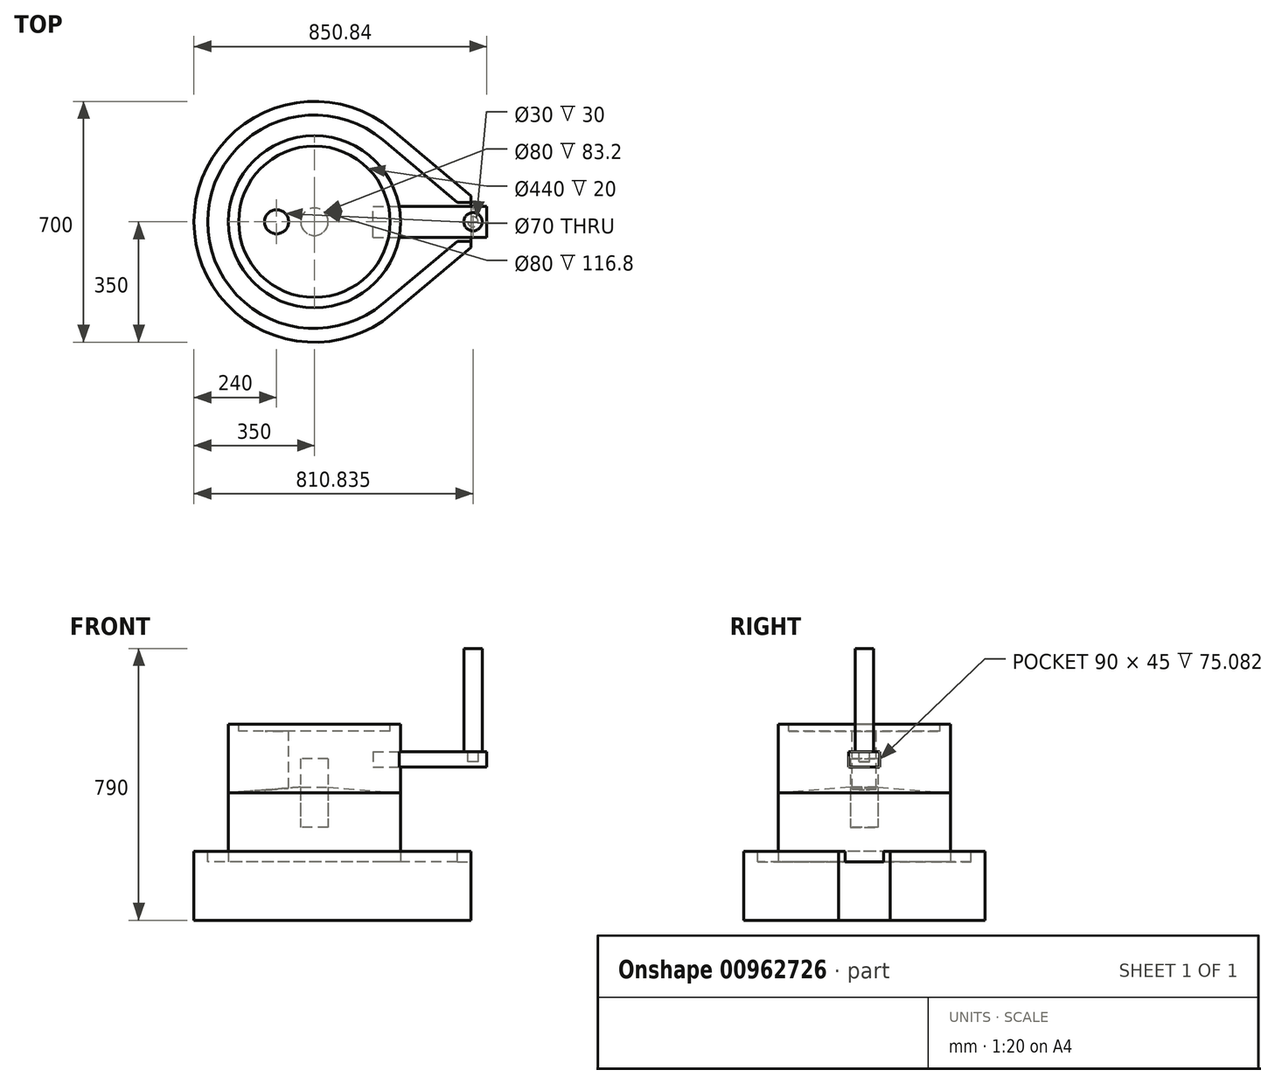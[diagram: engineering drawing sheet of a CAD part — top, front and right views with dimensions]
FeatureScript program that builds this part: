
annotation { "Feature Type Name" : "Feature", "Feature Type Description" : "" }
export const myFeature = defineFeature(function(context is Context, id is Id, definition is map)
    precondition{}
    {
        {
            var Q0;
            Q0=qCreatedBy(makeId("Top.planeOp"),FACE);
            var sketch = newSketch(context, id + "F0", { "sketchPlane" : qUnion([Q0])});
            skCircle(sketch, "E0", {"center": v(0, 0) * mm, "radius": 350 * mm});
            skLineSegment(sketch, "E1", {"start": v(454.84, 0) * mm, "end": v(454.84, 75) * mm});
            skLineSegment(sketch, "E2", {"start": v(454.84, 75) * mm, "end": v(225.14, 267.98) * mm});
            skLineSegment(sketch, "E3.MirrorCS", {"start": v(454.84, -75) * mm, "end": v(225.14, -267.98) * mm});
            skLineSegment(sketch, "E4.MirrorCS", {"start": v(454.84, 0) * mm, "end": v(454.84, -75) * mm});
            skSolve(sketch);
        }
        {
            var Q0;
            Q0=qSketchRegion(id+"F0",true);
            extrude(context, id + "F1", {"entities" : qUnion([Q0]), "depth" : 200 * mm, "offsetDistance" : 25 * mm});
        }
        {
            var Q0;
            Q0=makeQuery(id+"F1.opExtrude","CAP_FACE",FACE,{"disambiguationData":[OSD([sQuery(id+"F0.wireOp",EDGE,"E0"),sQuery(id+"F0.wireOp",EDGE,"E1"),sQuery(id+"F0.wireOp",EDGE,"E2"),sQuery(id+"F0.wireOp",EDGE,"E3.MirrorCS"),sQuery(id+"F0.wireOp",EDGE,"E4.MirrorCS")])],"isStart":false});
            var sketch = newSketch(context, id + "F2", { "sketchPlane" : qUnion([Q0])});
            skArc(sketch, "E5.0", {"start": v(199.4, 237.35) * mm, "mid": v(-310, 0) * mm, "end": v(199.4, -237.35) * mm});
            skLineSegment(sketch, "E5.1", {"start": v(414.84, 56.36) * mm, "end": v(199.4, 237.35) * mm});
            skLineSegment(sketch, "E5.3", {"start": v(199.4, -237.35) * mm, "end": v(414.84, -56.36) * mm});
            skLineSegment(sketch, "E6", {"start": v(414.84, 56.36) * mm, "end": v(454.84, 56.36) * mm});
            skLineSegment(sketch, "E7", {"start": v(454.84, 56.36) * mm, "end": v(454.84, -56.36) * mm});
            skLineSegment(sketch, "E8", {"start": v(454.84, -56.36) * mm, "end": v(414.84, -56.36) * mm});
            skSolve(sketch);
        }
        {
            var Q0;
            Q0=qSketchRegion(id+"F2",true);
            extrude(context, id + "F3", {"entities" : qUnion([Q0]), "operationType" : NewBodyOperationType.REMOVE, "oppositeDirection" : true, "depth" : 30 * mm, "offsetDistance" : 25 * mm});
        }
        {
            var Q0;
            Q0=makeQuery(id+"F3.boolean.opBoolean","COPY",FACE,{"derivedFrom":makeQuery(id+"F3.opExtrude","CAP_FACE",FACE,{"disambiguationData":[OSD([sQuery(id+"F2.wireOp",EDGE,"E5.0"),sQuery(id+"F2.wireOp",EDGE,"E5.1"),sQuery(id+"F2.wireOp",EDGE,"E5.3"),sQuery(id+"F2.wireOp",EDGE,"E6"),sQuery(id+"F2.wireOp",EDGE,"E7"),sQuery(id+"F2.wireOp",EDGE,"E8")])],"isStart":false})});
            var sketch = newSketch(context, id + "F4", { "sketchPlane" : qUnion([Q0])});
            skCircle(sketch, "E9", {"center": v(0, 0) * mm, "radius": 250 * mm});
            skSolve(sketch);
        }
        {
            var Q0;
            Q0=qSketchRegion(id+"F4",true);
            extrude(context, id + "F5", {"entities" : qUnion([Q0]), "depth" : 200 * mm, "offsetDistance" : 25 * mm});
        }
        {
            var Q0;
            Q0=qCreatedBy(makeId("Front.planeOp"),FACE);
            var sketch = newSketch(context, id + "F6", { "sketchPlane" : qUnion([Q0])});
            skLineSegment(sketch, "E10", {"start": v(0, 390) * mm, "end": v(0, 370) * mm});
            skLineSegment(sketch, "E11", {"start": v(0, 370) * mm, "end": v(-250, 370) * mm});
            skLineSegment(sketch, "E12", {"start": v(-250, 370) * mm, "end": v(0, 390) * mm});
            skSolve(sketch);
        }
        {
            var Q0;
            Q0=qSketchRegion(id+"F6",true);
            var Q1;
            Q1=sQuery(id+"F6.wireOp",EDGE,"E10");
            revolve(context, id + "F7", {"operationType" : NewBodyOperationType.ADD, "surfaceOperationType" : NewSurfaceOperationType.NEW, "entities" : qUnion([Q0]), "axis" : qUnion([Q1]), "revolveType" : RevolveType.FULL});
        }
        {
            var Q0;
            Q0=makeQuery(id+"F3.boolean.opBoolean","COPY",FACE,{"derivedFrom":makeQuery(id+"F3.opExtrude","CAP_FACE",FACE,{"disambiguationData":[OSD([sQuery(id+"F2.wireOp",EDGE,"E5.0"),sQuery(id+"F2.wireOp",EDGE,"E5.1"),sQuery(id+"F2.wireOp",EDGE,"E5.3"),sQuery(id+"F2.wireOp",EDGE,"E6"),sQuery(id+"F2.wireOp",EDGE,"E7"),sQuery(id+"F2.wireOp",EDGE,"E8")])],"isStart":false})});
            cPlane(context, id + "F8", {"entities" : qUnion([Q0]), "cplaneType" : CPlaneType.OFFSET, "offset" : 200 * mm, "width" : 150 * mm, "height" : 150 * mm});
        }
        {
            var Q0;
            Q0=qCreatedBy(id+"F8.planeOp",FACE);
            var sketch = newSketch(context, id + "F9", { "sketchPlane" : qUnion([Q0])});
            skCircle(sketch, "E13", {"center": v(0, 0) * mm, "radius": 40 * mm});
            skSolve(sketch);
        }
        {
            var Q0;
            Q0=qSketchRegion(id+"F9",true);
            extrude(context, id + "F10", {"entities" : qUnion([Q0]), "endBound" : BoundingType.SYMMETRIC, "depth" : 200 * mm, "offsetDistance" : 25 * mm});
        }
        {
            var Q0;
            Q0=qCreatedBy(id+"F8.planeOp",FACE);
            var sketch = newSketch(context, id + "F11", { "sketchPlane" : qUnion([Q0])});
            skCircle(sketch, "E14.0", {"center": v(0, 0) * mm, "radius": 250 * mm});
            skSolve(sketch);
        }
        {
            var Q0;
            Q0=makeQuery(id+"F10.opExtrude","SWEPT_BODY",BODY,{"disambiguationData":[OSD([sQuery(id+"F9.wireOp",EDGE,"E13")])]});
            var Q1;
            Q1=makeQuery(id+"F5.opExtrude","SWEPT_BODY",BODY,{"disambiguationData":[OSD([sQuery(id+"F4.wireOp",EDGE,"E9")])]});
            booleanBodies(context, id + "F12", {"operationType" : BooleanOperationType.SUBTRACTION, "tools" : qUnion([Q0]), "targets" : qUnion([Q1]), "keepTools" : true});
        }
        {
            var Q0;
            Q0=qSketchRegion(id+"F11",true);
            extrude(context, id + "F13", {"entities" : qUnion([Q0]), "depth" : 200 * mm, "offsetDistance" : 25 * mm});
        }
        {
            var Q0;
            Q0=makeQuery(id+"F10.opExtrude","SWEPT_BODY",BODY,{"disambiguationData":[OSD([sQuery(id+"F9.wireOp",EDGE,"E13")])]});
            var Q1;
            Q1=makeQuery(id+"F5.opExtrude","SWEPT_BODY",BODY,{"disambiguationData":[OSD([sQuery(id+"F4.wireOp",EDGE,"E9")])]});
            var Q2;
            Q2=makeQuery(id+"F13.opExtrude","SWEPT_BODY",BODY,{"disambiguationData":[OSD([sQuery(id+"F11.wireOp",EDGE,"E14.0")])]});
            booleanBodies(context, id + "F14", {"operationType" : BooleanOperationType.SUBTRACTION, "tools" : qUnion([Q0, Q1]), "targets" : qUnion([Q2]), "keepTools" : true});
        }
        {
            var Q0;
            Q0=makeQuery(id+"F13.opExtrude","CAP_FACE",FACE,{"disambiguationData":[OSD([sQuery(id+"F11.wireOp",EDGE,"E14.0")])],"isStart":false});
            var sketch = newSketch(context, id + "F15", { "sketchPlane" : qUnion([Q0])});
            skCircle(sketch, "E15.0", {"center": v(0, 0) * mm, "radius": 220 * mm});
            skSolve(sketch);
        }
        {
            var Q0;
            Q0=qSketchRegion(id+"F15",true);
            extrude(context, id + "F16", {"entities" : qUnion([Q0]), "operationType" : NewBodyOperationType.REMOVE, "oppositeDirection" : true, "depth" : 20 * mm, "offsetDistance" : 25 * mm});
        }
        {
            var Q0;
            Q0=makeQuery(id+"F16.boolean.opBoolean","COPY",FACE,{"derivedFrom":makeQuery(id+"F16.opExtrude","CAP_FACE",FACE,{"disambiguationData":[OSD([sQuery(id+"F15.wireOp",EDGE,"E15.0")])],"isStart":false})});
            var sketch = newSketch(context, id + "F17", { "sketchPlane" : qUnion([Q0])});
            skCircle(sketch, "E16", {"center": v(-110, 0) * mm, "radius": 35 * mm});
            skSolve(sketch);
        }
        {
            var Q0;
            Q0=qSketchRegion(id+"F17",true);
            var Q1;
            Q1=makeQuery(id+"F7.opRevolve","SWEPT_FACE",FACE,{"disambiguationData":[OSD([sQuery(id+"F6.wireOp",EDGE,"E12")])]});
            extrude(context, id + "F18", {"entities" : qUnion([Q0]), "operationType" : NewBodyOperationType.REMOVE, "endBound" : BoundingType.UP_TO_SURFACE, "oppositeDirection" : true, "depth" : 25 * mm, "endBoundEntityFace" : qUnion([Q1]), "offsetDistance" : 25 * mm});
        }
        {
            var Q0;
            Q0=makeQuery(id+"F1.opExtrude","SWEPT_FACE",FACE,{"disambiguationData":[OSD([sQuery(id+"F0.wireOp",EDGE,"E1"),sQuery(id+"F0.wireOp",EDGE,"E4.MirrorCS")])]});
            cPlane(context, id + "F19", {"entities" : qUnion([Q0]), "cplaneType" : CPlaneType.OFFSET, "offset" : 204 * mm, "oppositeDirection" : true, "width" : 150 * mm, "height" : 150 * mm});
        }
        {
            var Q0;
            Q0=qCreatedBy(id+"F19.planeOp",FACE);
            var sketch = newSketch(context, id + "F20", { "sketchPlane" : qUnion([Q0])});
            skLineSegment(sketch, "E17", {"start": v(-45, 490) * mm, "end": v(0, 490) * mm});
            skLineSegment(sketch, "E18", {"start": v(-45, 490) * mm, "end": v(-45, 445) * mm});
            skLineSegment(sketch, "E19", {"start": v(-45, 445) * mm, "end": v(0, 445) * mm});
            skLineSegment(sketch, "E20.MirrorCS", {"start": v(45, 490) * mm, "end": v(0, 490) * mm});
            skLineSegment(sketch, "E21.MirrorCS", {"start": v(45, 490) * mm, "end": v(45, 445) * mm});
            skLineSegment(sketch, "E22.MirrorCS", {"start": v(45, 445) * mm, "end": v(0, 445) * mm});
            skSolve(sketch);
        }
        {
            var Q0;
            Q0=qSketchRegion(id+"F20",true);
            extrude(context, id + "F21", {"entities" : qUnion([Q0]), "oppositeDirection" : true, "depth" : 80 * mm, "offsetDistance" : 25 * mm});
        }
        {
            var Q0;
            Q0=makeQuery(id+"F21.opExtrude","CAP_FACE",FACE,{"disambiguationData":[OSD([sQuery(id+"F20.wireOp",EDGE,"E17"),sQuery(id+"F20.wireOp",EDGE,"E18"),sQuery(id+"F20.wireOp",EDGE,"E19"),sQuery(id+"F20.wireOp",EDGE,"E20.MirrorCS"),sQuery(id+"F20.wireOp",EDGE,"E21.MirrorCS"),sQuery(id+"F20.wireOp",EDGE,"E22.MirrorCS")])],"isStart":true});
            var sketch = newSketch(context, id + "F22", { "sketchPlane" : qUnion([Q0])});
            skLineSegment(sketch, "E23.bottom", {"start": v(-45, 490) * mm, "end": v(45, 490) * mm});
            skLineSegment(sketch, "E23.top", {"start": v(-45, 445) * mm, "end": v(45, 445) * mm});
            skLineSegment(sketch, "E23.left", {"start": v(-45, 490) * mm, "end": v(-45, 445) * mm});
            skLineSegment(sketch, "E23.right", {"start": v(45, 490) * mm, "end": v(45, 445) * mm});
            skSolve(sketch);
        }
        {
            var Q0;
            Q0=qSketchRegion(id+"F22",true);
            extrude(context, id + "F23", {"entities" : qUnion([Q0]), "operationType" : NewBodyOperationType.ADD, "depth" : 250 * mm, "offsetDistance" : 25 * mm});
        }
        {
            var Q0;
            Q0=makeQuery(id+"F23.boolean.opBoolean","MERGE",FACE,{"derivedFrom":[makeQuery(id+"F21.opExtrude","SWEPT_FACE",FACE,{"disambiguationData":[OSD([sQuery(id+"F20.wireOp",EDGE,"E17"),sQuery(id+"F20.wireOp",EDGE,"E20.MirrorCS")])]}),makeQuery(id+"F23.opExtrude","SWEPT_FACE",FACE,{"disambiguationData":[OSD([sQuery(id+"F22.wireOp",EDGE,"E23.bottom")])]})]});
            var sketch = newSketch(context, id + "F24", { "sketchPlane" : qUnion([Q0])});
            skCircle(sketch, "E24", {"center": v(460.84, 0) * mm, "radius": 15 * mm});
            skSolve(sketch);
        }
        {
            var Q0;
            Q0=qSketchRegion(id+"F24",true);
            extrude(context, id + "F25", {"entities" : qUnion([Q0]), "oppositeDirection" : true, "depth" : 30 * mm, "offsetDistance" : 25 * mm});
        }
        {
            var Q0;
            Q0=makeQuery(id+"F25.opExtrude","SWEPT_BODY",BODY,{"disambiguationData":[OSD([sQuery(id+"F24.wireOp",EDGE,"E24")])]});
            var Q1;
            Q1=makeQuery(id+"F21.opExtrude","SWEPT_BODY",BODY,{"disambiguationData":[OSD([sQuery(id+"F20.wireOp",EDGE,"E17"),sQuery(id+"F20.wireOp",EDGE,"E18"),sQuery(id+"F20.wireOp",EDGE,"E19"),sQuery(id+"F20.wireOp",EDGE,"E20.MirrorCS"),sQuery(id+"F20.wireOp",EDGE,"E21.MirrorCS"),sQuery(id+"F20.wireOp",EDGE,"E22.MirrorCS")])]});
            booleanBodies(context, id + "F26", {"operationType" : BooleanOperationType.SUBTRACTION, "tools" : qUnion([Q0]), "targets" : qUnion([Q1]), "keepTools" : true});
        }
        {
            var Q0;
            Q0=makeQuery(id+"F25.opExtrude","CAP_FACE",FACE,{"disambiguationData":[OSD([sQuery(id+"F24.wireOp",EDGE,"E24")])],"isStart":true});
            var sketch = newSketch(context, id + "F27", { "sketchPlane" : qUnion([Q0])});
            skCircle(sketch, "E25", {"center": v(460.84, 0) * mm, "radius": 26.57 * mm});
            skSolve(sketch);
        }
        {
            var Q0;
            Q0=qSketchRegion(id+"F27",true);
            extrude(context, id + "F28", {"entities" : qUnion([Q0]), "depth" : 300 * mm, "offsetDistance" : 25 * mm});
        }
        {
            var Q0;
            Q0=makeQuery(id+"F21.opExtrude","SWEPT_BODY",BODY,{"disambiguationData":[OSD([sQuery(id+"F20.wireOp",EDGE,"E17"),sQuery(id+"F20.wireOp",EDGE,"E18"),sQuery(id+"F20.wireOp",EDGE,"E19"),sQuery(id+"F20.wireOp",EDGE,"E20.MirrorCS"),sQuery(id+"F20.wireOp",EDGE,"E21.MirrorCS"),sQuery(id+"F20.wireOp",EDGE,"E22.MirrorCS")])]});
            var Q1;
            Q1=makeQuery(id+"F13.opExtrude","SWEPT_BODY",BODY,{"disambiguationData":[OSD([sQuery(id+"F11.wireOp",EDGE,"E14.0")])]});
            booleanBodies(context, id + "F29", {"operationType" : BooleanOperationType.SUBTRACTION, "tools" : qUnion([Q0]), "targets" : qUnion([Q1]), "keepTools" : true});
        }
    });
